# Revit family: Door_Barn_Stone
name_source: partatom
category: Doors
units: mm (PartAtom-declared; Revit-internal decimal feet)

## family parameters
Always vertical = Yes
Classification Number = 23.30.10.17.11
Cut with Voids When Loaded = No
Host = Wall
Room Calculation Point = No
Shared = No

## types (3) — shared parameters
Air Space Beneath Door = 0' - 0 7/16"
Analytic Construction = <None>
Assembly Code = C1020100
Description = Renin Barn Door and Track - Stone Easy Slide Soft Close as Specified
Door Design = Door_Barn-Panel_Renin_K : Grooved Wood Panel
Fire Rating = As Specified
Function = Interior
Keynote = 08 00 00
Manufacturer = Renin Corp
Manufacturer Fax = 905-791-3813
Manufacturer Website = https://www.renin.com
Maximum Width = 0' - 0"
Minimum Width = 0' - 0"
Panel Height = 7' - 0"
Panel Thickness = 0' - 1 3/8"
Panel Width = 3' - 0"
Product Data = http://www.arcat.com
Sales Information = https://www.renin.com
Thickness = 0' - 0"
Track Width = 8' - 0"
Type Comments = Confirm Opening Size Requirements
URL = https://www.renin.com
Wall Closure = By host
longtrackmounts = Yes
zero-valued in all types: Expected Lifespan (Years), Maintenance Schedule (Months), Sound Transmission Class (STC), Warranty Duration (Years)

## per-type parameters (varying)
| type | Model |
| Off-White | Stone - Off-White |
| Iron Age Grey | Stone - Iron Age Grey |
| Sandstone | Stone - Sandstone |

## geometry (parser evidence)
native form markers: Blend x16, Sweep x7
no freeform markers — native parametric forms only
